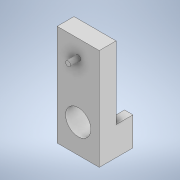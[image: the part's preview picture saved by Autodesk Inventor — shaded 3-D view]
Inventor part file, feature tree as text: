
AUTODESK INVENTOR PART (.ipt)
format: ipt  version: 2021 (Build 250183000, 183)  size: 329,728 bytes
history: native  units: mm
features: sketch x5, extrude x4, thread x1, emboss x1
ambient origin geometry x8: Origin, YZ Plane, XZ Plane, XY Plane, X Axis, Y Axis, Z Axis, Center Point
bodies: Solid1 (feature_tree)
feature tree (11):
  extrude  "Extrusion1"  Depth=25.0mm
  extrude  "Extrusion2"  Depth=12.5mm
  thread  "Thread1"  [1 undecoded]
  extrude  "Extrusion3"  Depth=6.0mm TaperAngle=0.0deg
  extrude  "Extrusion5"  Depth=10.0mm TaperAngle=0.0deg
  emboss  "Emboss1"
  sketch  "Sketch1"  dims[d0=60.0mm d1=25.0mm]
  sketch  "Sketch2"  dims[d2=12.5mm d5=12.5mm d6=10.0mm d7=0.0mm]
  sketch  "Sketch3"  dims[d8=3.0mm d10=6.0mm d11=0.0mm]
  sketch  "Sketch5"  dims[d12=6.0mm d13=0.0mm d15=10.0mm d16=0.0mm]
  sketch  "Sketch6"  dims[d20=17.0mm d21=5.0mm d22=5.0mm d25=7.5mm d26=15.0mm d27=10.0mm d28=0.0mm d29=37.5mm d30=1.0mm d31=0.0mm d9=0.872665mm]
note: 1 required parameter value undecoded (feature->parameter linkage not recoverable at this tier; creation-order binding heuristic only, values carry confidence <= 0.55)
